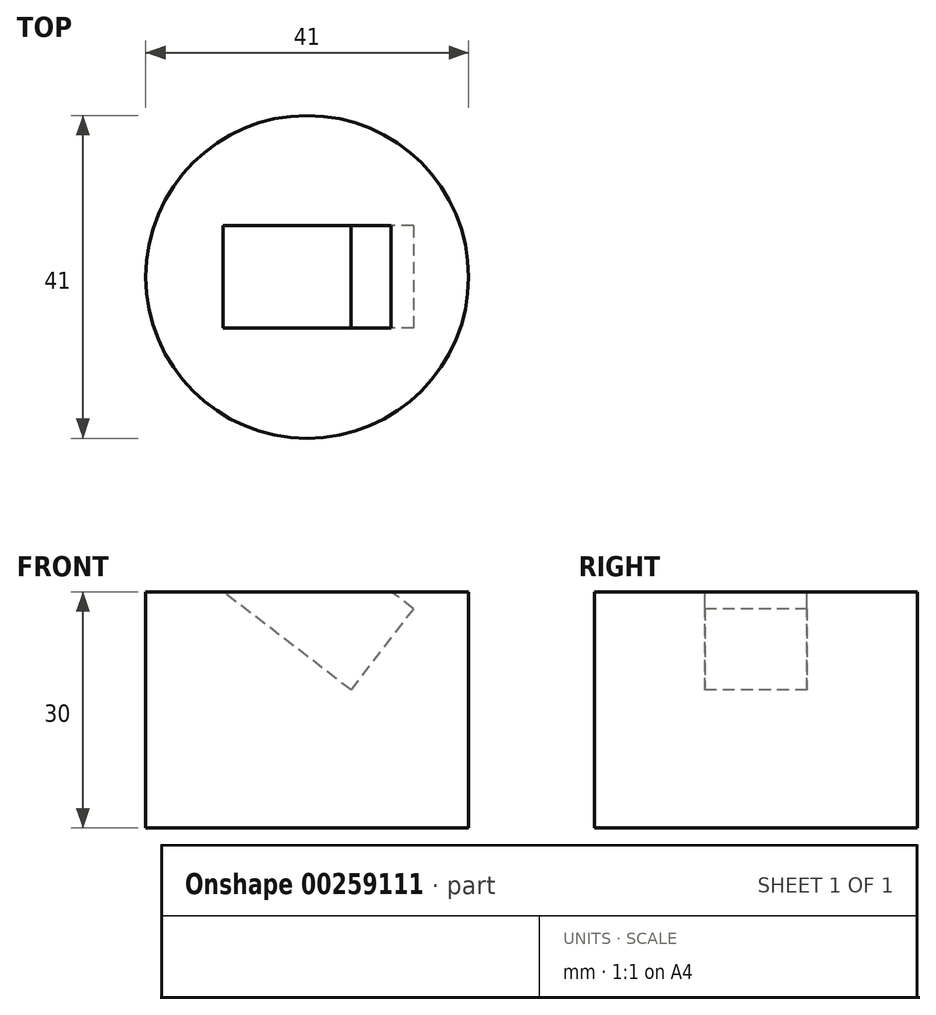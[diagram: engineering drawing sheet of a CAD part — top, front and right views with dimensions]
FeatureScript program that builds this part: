
annotation { "Feature Type Name" : "Feature", "Feature Type Description" : "" }
export const myFeature = defineFeature(function(context is Context, id is Id, definition is map)
    precondition{}
    {
        {
            var Q0;
            Q0=qCreatedBy(makeId("Top.planeOp"),FACE);
            var sketch = newSketch(context, id + "F0", { "sketchPlane" : qUnion([Q0])});
            skCircle(sketch, "E0", {"center": v(0, 0) * mm, "radius": 20.5 * mm});
            skSolve(sketch);
        }
        {
            var Q0;
            Q0 = qSketchRegion(id + "F0", true);
            extrude(context, id + "F1", {"entities" : qUnion([Q0]), "depth" : 15 * mm, "hasSecondDirection" : true, "secondDirectionOppositeDirection" : true, "secondDirectionDepth" : 15 * mm});
        }
        {
            var Q0;
            Q0=qCreatedBy(makeId("Front.planeOp"),FACE);
            var sketch = newSketch(context, id + "F2", { "sketchPlane" : qUnion([Q0])});
            skLineSegment(sketch, "E1", {"start": v(0, 0) * mm, "end": v(0, 15) * mm});
            skLineSegment(sketch, "E2", {"start": v(7.93, 8.91) * mm, "end": v(0, 15) * mm});
            skLineSegment(sketch, "E3", {"start": v(0, 15) * mm, "end": v(-15.36, 26.79) * mm});
            skLineSegment(sketch, "E4.0", {"start": v(18.05, 9.34) * mm, "end": v(-11.4, 31.94) * mm});
            skLineSegment(sketch, "E5.0", {"start": v(9.87, -0.77) * mm, "end": v(-19.32, 21.63) * mm});
            skLineSegment(sketch, "E6", {"start": v(13.48, 12.85) * mm, "end": v(5.56, 2.54) * mm});
            skLineSegment(sketch, "E7", {"start": v(-11.4, 31.94) * mm, "end": v(-19.32, 21.63) * mm});
            skSolve(sketch);
        }
        {
            var Q0;
            Q0 = qSketchRegion(id + "F2", true);
            extrude(context, id + "F3", {"entities" : qUnion([Q0]), "operationType" : NewBodyOperationType.REMOVE, "oppositeDirection" : true, "depth" : 6.5 * mm, "hasSecondDirection" : true, "secondDirectionOppositeDirection" : false, "secondDirectionDepth" : 6.5 * mm});
        }
    });
